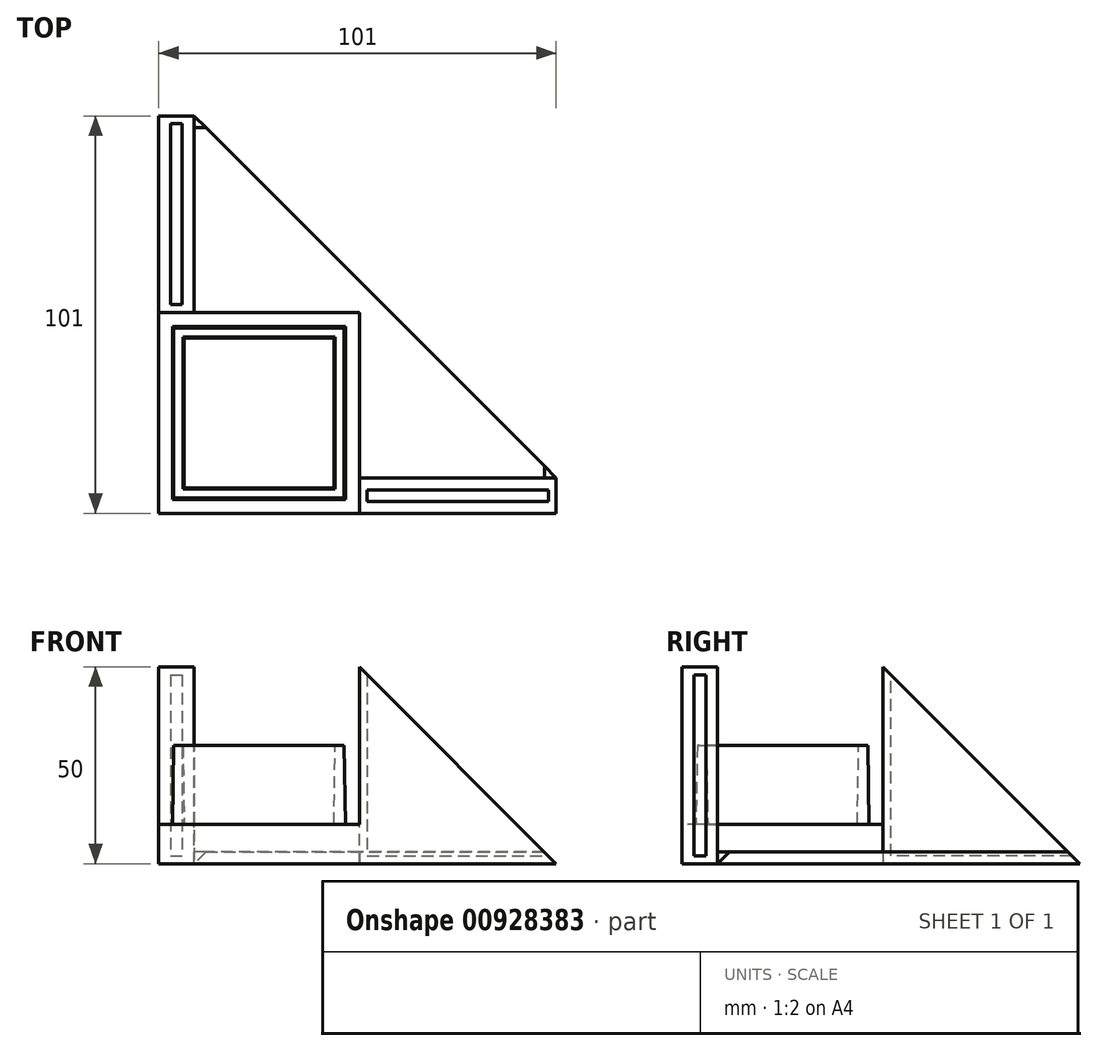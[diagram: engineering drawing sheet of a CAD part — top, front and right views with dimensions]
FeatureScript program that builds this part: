
annotation { "Feature Type Name" : "Feature", "Feature Type Description" : "" }
export const myFeature = defineFeature(function(context is Context, id is Id, definition is map)
    precondition{}
    {
        {
            var Q0;
            Q0=qCreatedBy(makeId("Top.planeOp"),FACE);
            var sketch = newSketch(context, id + "F0", { "sketchPlane" : qUnion([Q0])});
            skLineSegment(sketch, "E0.bottom", {"start": v(25.5, 25.5) * mm, "end": v(-25.5, 25.5) * mm});
            skLineSegment(sketch, "E0.top", {"start": v(25.5, -25.5) * mm, "end": v(-25.5, -25.5) * mm});
            skLineSegment(sketch, "E0.left", {"start": v(25.5, 25.5) * mm, "end": v(25.5, -25.5) * mm});
            skLineSegment(sketch, "E0.right", {"start": v(-25.5, 25.5) * mm, "end": v(-25.5, -25.5) * mm});
            skPoint(sketch, "E0.middle", {"position": v(0, 0) * mm});
            skSolve(sketch);
        }
        {
            var Q0;
            Q0=makeQuery(id+"F0.imprint","IMPRINT",FACE,{"disambiguationData":[TD([[makeQuery(id+"F0.imprint","IMPRINT",EDGE,{"derivedFrom":sQuery(id+"F0.wireOp",EDGE,"E0.bottom")}),1.0]])]});
            extrude(context, id + "F1", {"entities" : qUnion([Q0]), "depth" : 10 * mm, "offsetDistance" : 25 * mm});
        }
        {
            var Q0;
            Q0=qCreatedBy(makeId("Front.planeOp"),FACE);
            cPlane(context, id + "F2", {"entities" : qUnion([Q0]), "cplaneType" : CPlaneType.OFFSET, "offset" : 21 * mm, "width" : 150 * mm, "height" : 150 * mm});
        }
        {
            var Q0;
            Q0=qCreatedBy(id+"F2.planeOp",FACE);
            var sketch = newSketch(context, id + "F3", { "sketchPlane" : qUnion([Q0])});
            skLineSegment(sketch, "E1", {"start": v(25.5, 0) * mm, "end": v(25.5, 50) * mm});
            skLineSegment(sketch, "E2", {"start": v(25.5, 50) * mm, "end": v(75.5, 0) * mm});
            skLineSegment(sketch, "E3", {"start": v(75.5, 0) * mm, "end": v(25.5, 0) * mm});
            skSolve(sketch);
        }
        {
            var Q0;
            Q0=makeQuery(id+"F3.imprint","IMPRINT",FACE,{"disambiguationData":[TD([[makeQuery(id+"F3.imprint","IMPRINT",EDGE,{"derivedFrom":sQuery(id+"F3.wireOp",EDGE,"E1")}),-1.0]])]});
            extrude(context, id + "F4", {"entities" : qUnion([Q0]), "operationType" : NewBodyOperationType.ADD, "endBound" : BoundingType.SYMMETRIC, "depth" : 9 * mm, "offsetDistance" : 25 * mm});
        }
        {
            var Q0;
            Q0=qCreatedBy(id+"F2.planeOp",FACE);
            var sketch = newSketch(context, id + "F5", { "sketchPlane" : qUnion([Q0])});
            skLineSegment(sketch, "E4", {"start": v(27.5, 48) * mm, "end": v(27.5, 2) * mm});
            skLineSegment(sketch, "E5", {"start": v(27.5, 2) * mm, "end": v(73.5, 2) * mm});
            skLineSegment(sketch, "E6", {"start": v(73.5, 2) * mm, "end": v(27.5, 48) * mm});
            skSolve(sketch);
        }
        {
            var Q0;
            Q0 = qSketchRegion(id + "F5", true);
            extrude(context, id + "F6", {"entities" : qUnion([Q0]), "operationType" : NewBodyOperationType.REMOVE, "endBound" : BoundingType.SYMMETRIC, "depth" : 3 * mm, "offsetDistance" : 25 * mm});
        }
        {
            var Q0;
            Q0=qCreatedBy(makeId("Right.planeOp"),FACE);
            cPlane(context, id + "F7", {"entities" : qUnion([Q0]), "cplaneType" : CPlaneType.OFFSET, "offset" : 21 * mm, "oppositeDirection" : true, "width" : 150 * mm, "height" : 150 * mm});
        }
        {
            var Q0;
            Q0=qCreatedBy(id+"F7.planeOp",FACE);
            var sketch = newSketch(context, id + "F8", { "sketchPlane" : qUnion([Q0])});
            skLineSegment(sketch, "E7", {"start": v(25.5, 0) * mm, "end": v(25.5, 50) * mm});
            skLineSegment(sketch, "E8", {"start": v(25.5, 50) * mm, "end": v(75.5, 0) * mm});
            skLineSegment(sketch, "E9", {"start": v(75.5, 0) * mm, "end": v(25.5, 0) * mm});
            skSolve(sketch);
        }
        {
            var Q0;
            Q0=makeQuery(id+"F8.imprint","IMPRINT",FACE,{"disambiguationData":[TD([[makeQuery(id+"F8.imprint","IMPRINT",EDGE,{"derivedFrom":sQuery(id+"F8.wireOp",EDGE,"E7")}),-1.0]])]});
            extrude(context, id + "F9", {"entities" : qUnion([Q0]), "operationType" : NewBodyOperationType.ADD, "endBound" : BoundingType.SYMMETRIC, "depth" : 9 * mm, "offsetDistance" : 25 * mm});
        }
        {
            var Q0;
            Q0=qCreatedBy(id+"F7.planeOp",FACE);
            var sketch = newSketch(context, id + "F10", { "sketchPlane" : qUnion([Q0])});
            skLineSegment(sketch, "E10", {"start": v(27.5, 2) * mm, "end": v(27.5, 48) * mm});
            skLineSegment(sketch, "E11", {"start": v(27.5, 48) * mm, "end": v(73.5, 2) * mm});
            skLineSegment(sketch, "E12", {"start": v(73.5, 2) * mm, "end": v(27.5, 2) * mm});
            skSolve(sketch);
        }
        {
            var Q0;
            Q0 = qSketchRegion(id + "F10", true);
            extrude(context, id + "F11", {"entities" : qUnion([Q0]), "operationType" : NewBodyOperationType.REMOVE, "endBound" : BoundingType.SYMMETRIC, "oppositeDirection" : true, "depth" : 3 * mm, "offsetDistance" : 25 * mm});
        }
        {
            var Q0;
            Q0=makeQuery(id+"F1.opExtrude","CAP_FACE",FACE,{"disambiguationData":[OSD([sQuery(id+"F0.wireOp",EDGE,"E0.bottom"),sQuery(id+"F0.wireOp",EDGE,"E0.top"),sQuery(id+"F0.wireOp",EDGE,"E0.left"),sQuery(id+"F0.wireOp",EDGE,"E0.right")])],"isStart":false});
            var sketch = newSketch(context, id + "F12", { "sketchPlane" : qUnion([Q0])});
            skLineSegment(sketch, "E13.bottom", {"start": v(22, 22) * mm, "end": v(-22, 22) * mm});
            skLineSegment(sketch, "E13.top", {"start": v(22, -22) * mm, "end": v(-22, -22) * mm});
            skLineSegment(sketch, "E13.left", {"start": v(22, 22) * mm, "end": v(22, -22) * mm});
            skLineSegment(sketch, "E13.right", {"start": v(-22, 22) * mm, "end": v(-22, -22) * mm});
            skPoint(sketch, "E13.middle", {"position": v(0, 0) * mm});
            skLineSegment(sketch, "E14.bottom", {"start": v(19, 19) * mm, "end": v(-19, 19) * mm});
            skLineSegment(sketch, "E14.top", {"start": v(19, -19) * mm, "end": v(-19, -19) * mm});
            skLineSegment(sketch, "E14.left", {"start": v(19, 19) * mm, "end": v(19, -19) * mm});
            skLineSegment(sketch, "E14.right", {"start": v(-19, 19) * mm, "end": v(-19, -19) * mm});
            skSolve(sketch);
        }
        {
            var Q0;
            Q0=makeQuery(id+"F12.imprint","IMPRINT",FACE,{"disambiguationData":[TD([[makeQuery(id+"F12.imprint","IMPRINT",EDGE,{"derivedFrom":sQuery(id+"F12.wireOp",EDGE,"E13.bottom")}),1.0]])]});
            extrude(context, id + "F13", {"entities" : qUnion([Q0]), "operationType" : NewBodyOperationType.ADD, "depth" : 20 * mm, "offsetDistance" : 25 * mm, "hasDraft" : true, "draftAngle" : 1 * degree, "draftPullDirection" : true});
        }
        {
            var Q0;
            Q0=makeQuery(id+"F9.boolean.opBoolean","MERGE",FACE,{"derivedFrom":[makeQuery(id+"F4.boolean.opBoolean","MERGE",FACE,{"derivedFrom":[makeQuery(id+"F1.opExtrude","CAP_FACE",FACE,{"disambiguationData":[OSD([sQuery(id+"F0.wireOp",EDGE,"E0.bottom"),sQuery(id+"F0.wireOp",EDGE,"E0.top"),sQuery(id+"F0.wireOp",EDGE,"E0.left"),sQuery(id+"F0.wireOp",EDGE,"E0.right")])],"isStart":true}),makeQuery(id+"F4.opExtrude","SWEPT_FACE",FACE,{"disambiguationData":[OSD([sQuery(id+"F3.wireOp",EDGE,"E3")])]})]}),makeQuery(id+"F9.opExtrude","SWEPT_FACE",FACE,{"disambiguationData":[OSD([sQuery(id+"F8.wireOp",EDGE,"E9")])]})]});
            var sketch = newSketch(context, id + "F14", { "sketchPlane" : qUnion([Q0])});
            skLineSegment(sketch, "E15", {"start": v(-16.5, -75.5) * mm, "end": v(75.5, 16.5) * mm});
            skLineSegment(sketch, "E16", {"start": v(75.5, 16.5) * mm, "end": v(25.5, 16.5) * mm});
            skLineSegment(sketch, "E17", {"start": v(25.5, 16.5) * mm, "end": v(25.5, -25.5) * mm});
            skLineSegment(sketch, "E18", {"start": v(25.5, -25.5) * mm, "end": v(-16.5, -25.5) * mm});
            skLineSegment(sketch, "E19", {"start": v(-16.5, -25.5) * mm, "end": v(-16.5, -75.5) * mm});
            skSolve(sketch);
        }
        {
            var Q0;
            Q0=makeQuery(id+"F14.imprint","IMPRINT",FACE,{"disambiguationData":[TD([[makeQuery(id+"F14.imprint","IMPRINT",EDGE,{"derivedFrom":sQuery(id+"F14.wireOp",EDGE,"E15")}),1.0]])]});
            extrude(context, id + "F15", {"entities" : qUnion([Q0]), "oppositeDirection" : true, "depth" : 3 * mm, "offsetDistance" : 25 * mm});
        }
        {
            var Q0;
            Q0=makeQuery(id+"F15.opExtrude","SWEPT_FACE",FACE,{"disambiguationData":[OSD([sQuery(id+"F14.wireOp",EDGE,"E19")])]});
            var sketch = newSketch(context, id + "F16", { "sketchPlane" : qUnion([Q0])});
            skLineSegment(sketch, "E20", {"start": v(-75.5, 3) * mm, "end": v(-75.5, 0) * mm});
            skLineSegment(sketch, "E21", {"start": v(-75.5, 0) * mm, "end": v(-72.5, 3) * mm});
            skLineSegment(sketch, "E22", {"start": v(-72.5, 3) * mm, "end": v(-75.5, 3) * mm});
            skSolve(sketch);
        }
        {
            var Q0;
            Q0=makeQuery(id+"F16.imprint","IMPRINT",FACE,{"disambiguationData":[TD([[makeQuery(id+"F16.imprint","IMPRINT",EDGE,{"derivedFrom":sQuery(id+"F16.wireOp",EDGE,"E20")}),1.0]])]});
            extrude(context, id + "F17", {"entities" : qUnion([Q0]), "operationType" : NewBodyOperationType.REMOVE, "oppositeDirection" : true, "depth" : 25 * mm, "offsetDistance" : 25 * mm});
        }
        {
            var Q0;
            Q0=makeQuery(id+"F15.opExtrude","SWEPT_FACE",FACE,{"disambiguationData":[OSD([sQuery(id+"F14.wireOp",EDGE,"E16")])]});
            var sketch = newSketch(context, id + "F18", { "sketchPlane" : qUnion([Q0])});
            skLineSegment(sketch, "E23", {"start": v(75.5, 3) * mm, "end": v(75.5, 0) * mm});
            skLineSegment(sketch, "E24", {"start": v(75.5, 0) * mm, "end": v(72.5, 3) * mm});
            skLineSegment(sketch, "E25", {"start": v(72.5, 3) * mm, "end": v(75.5, 3) * mm});
            skSolve(sketch);
        }
        {
            var Q0;
            Q0=makeQuery(id+"F18.imprint","IMPRINT",FACE,{"disambiguationData":[TD([[makeQuery(id+"F18.imprint","IMPRINT",EDGE,{"derivedFrom":sQuery(id+"F18.wireOp",EDGE,"E23")}),-1.0]])]});
            extrude(context, id + "F19", {"entities" : qUnion([Q0]), "operationType" : NewBodyOperationType.REMOVE, "oppositeDirection" : true, "depth" : 25 * mm, "offsetDistance" : 25 * mm});
        }
    });
